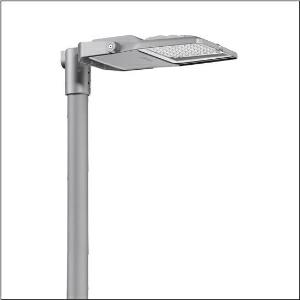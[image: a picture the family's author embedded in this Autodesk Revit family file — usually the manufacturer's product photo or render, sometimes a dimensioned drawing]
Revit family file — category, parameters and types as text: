
# Revit family: floodlight_fl_21_iq_mini___pl52_5xa7772d2d3a_9966
name_source: partatom
category: Lighting Fixtures
units: mm (PartAtom-declared; Revit-internal decimal feet)

## family parameters
Cut with Voids When Loaded = No
Host = Face
Light Source = No
Part Type = Normal
Room Calculation Point = No
Round Connector Dimension = Use Diameter
Shared = No

## types (1)
- --- (1 x LED, 17830 lm, 143 W, 3000K)
    Apparent Load = 143 VA
    CIE Flux Codes = 26 60 98 100 100
    Color Rendering = 70
    Color Temperature = 3000K
    Default Elevation = 1800 mm
    Description = Floodlight FL 21 iQ mini, floodlight, primary light control with lens, of PMMA, primary optical cover: protective disc, of toughened safety glass, transparent, light distribution: PL52, light emission: direct distribution, installation type: surface-mounted, LED, High Power LED, rated luminous flux: 17.830lm, luminous efficacy: 125lm/W, light colour: 730, colour temperature: 3000K, control: Auto-Match, Temp-Guard, Night-Set, Smart-Wire, Desk-Remote (wireless, voltage-free reading and setting of iQ features in the workshop via application-optimized NFC function/RFID function), optimised constant luminous flux control (CLO 2.0), Light-Fading, Lumen-Switch, with terminal, 6-pole, mains connection: 220..240V, AC, 50/60Hz, start of lifetime: 143W, end of service life: 152W, reduction: 61W, luminaire housing, of diecast aluminium, powder-coated, Siteco® metallic grey (DB 702S), corrosivity category C5 mid according to DIN EN ISO 12944, sealing non-destructively replaceable, please order mast flange separately, mast bracket, of steel, galvanised, powder-coated, protection rating (complete): IP66, insulation class (complete): insulation class II (safety insulation), certification: CE, ENEC, VDE, protection symbol: D, impact resistance: IK08, permissible operating ambient temperature: -40..+40°C, permissible operating ambient temperature for outdoor applications: -40..+50°C, standard: DIN EN 12944, LABS conformity tested according to VDMA 24364:2018-05, packaging unit: 1 piece

Light Distribution: PL52
    Height = 70 mm
    Lamp = 1 x LED
    Lamp Light Flux = 17830 lm
    Lamp Power = 143 W
    Lamp count = 1
    Length = 485 mm
    Luminous efficacy = 125 lm/W
    Manufacturer = Siteco
    ModVariant = No
    Model = 5XA7772D2D3A
    Number of Poles = 1
    OnlyDefault = Yes
    Power Factor = 1
    Product Name = Floodlight FL 21 iQ mini | PL52
    Product group = floodlight | pylon annexe
    ProductGroupID = 6200
    Protection Class = Protection class II
    Protection Degree = IP 66
    RLX_Detail_Level = 1
    RLX_Emergency_Light_Flux = 0 lm
    RLX_Emergency_Type = 0
    RLX_Emergency_Type_DB = No
    RlxData = <blob elided: 101697 chars, md5=524bd0e1>
    Socket = socket
    Standby Power = 0 W
    System Light Flux = 17830 lm
    System Power = 143 W
    Type Comments = factory setting: luminous flux: 100 % | dim-lin: 254 | 730 mA
    Type Image = l_1007125.jpg
    URL = http://relux.com
    VarID = @adj_096011
    Voltage = 0 V
    Weight = 0.00 kg
    Width = 337 mm

## geometry (parser evidence)
native form markers: Blend x4, Sweep x13
no freeform markers — native parametric forms only
